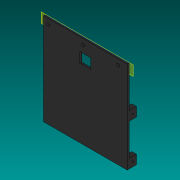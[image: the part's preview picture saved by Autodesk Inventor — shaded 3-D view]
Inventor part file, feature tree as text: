
AUTODESK INVENTOR PART (.ipt)
format: ipt  version: 2019 (Build 230136000, 136)  size: 189,952 bytes
history: native  units: mm
features: sketch x11, extrude x8, reference x8, other x3, plane x1
ambient origin geometry x8: Origin, YZ Plane, XZ Plane, XY Plane, X Axis, Y Axis, Z Axis, Center Point
bodies: Solid1 (feature_tree)
feature tree (31):
  plane  "Work Plane1"
  extrude  "Extrusion1"  Depth=100.0mm
  sketch  "Sketch2"  dims[d2=1.0mm d3=1.0mm]
  sketch  "Sketch3"  dims[d4=1.0mm d5=2.0mm d6=0.0mm]
  extrude  "Extrusion2"  Depth=1.0mm
  extrude  "Extrusion3"  Depth=2.0mm TaperAngle=0.0deg
  extrude  "Extrusion4"  Depth=4.0mm
  extrude  "Extrusion5"  Depth=8.0mm
  extrude  "Extrusion6"  Depth=8.0mm
  sketch  "Sketch9"  dims[d20=5.0mm d21=0.0mm]
  extrude  "Extrusion7"  Depth=8.0mm
  extrude  "Extrusion8"  Depth=10.0mm
  sketch  "Sketch1"  dims[d0=91.0mm d1=100.0mm]
  reference  "Reference1"
  reference  "Reference2"
  reference  "Reference3"
  reference  "Reference4"
  reference  "Reference5"
  reference  "Reference6"
  reference  "Reference7"
  reference  "Reference8"
  sketch  "Sketch4"  dims[d8=1.5mm d9=4.0mm]
  sketch  "Sketch5"  dims[d10=5.0mm d11=8.0mm]
  sketch  "Sketch6"  dims[d12=10.0mm d13=8.0mm]
  sketch  "Sketch7"  dims[d14=5.0mm d15=0.0mm d16=8.0mm]
  sketch  "Sketch8"  dims[d17=10.0mm d19=1.5mm]
  sketch  "Sketch10"  dims[d22=10.0mm]
  sketch  "Sketch11"  dims[d23=8.0mm d25=1.5mm d26=5.0mm d27=0.0mm d28=5.0mm d29=0.0mm d30=5.0mm d31=0.0mm d32=10.0mm d33=8.0mm d35=1.5mm d36=5.0mm d37=0.0mm d39=1.5mm d40=4.0mm d41=5.0mm d42=8.0mm d43=10.0mm d44=8.0mm d45=5.0mm d46=0.0mm]
  other  "Ensamblaje Reloj LCD 16x2.iam"
  other  "Down:1"
  other  "PCB Down:1"
